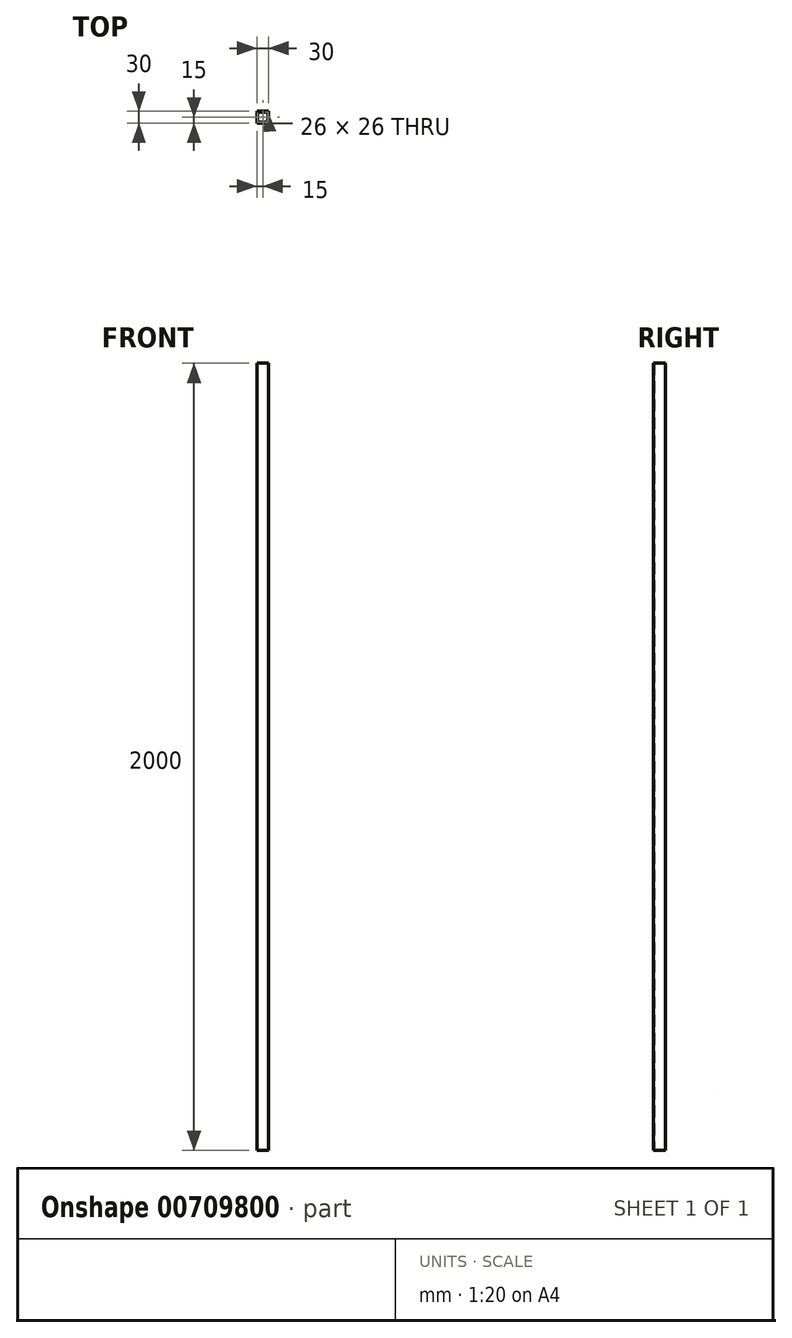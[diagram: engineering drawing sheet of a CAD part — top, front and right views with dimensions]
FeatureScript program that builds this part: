
annotation { "Feature Type Name" : "Feature", "Feature Type Description" : "" }
export const myFeature = defineFeature(function(context is Context, id is Id, definition is map)
    precondition{}
    {
        {
            var Q0;
            Q0=qCreatedBy(makeId("Top.planeOp"),FACE);
            var sketch = newSketch(context, id + "F0", { "sketchPlane" : qUnion([Q0])});
            skLineSegment(sketch, "E0.bottom", {"start": v(0, 0) * mm, "end": v(-30, 0) * mm});
            skLineSegment(sketch, "E0.top", {"start": v(0, 30) * mm, "end": v(-30, 30) * mm});
            skLineSegment(sketch, "E0.left", {"start": v(0, 0) * mm, "end": v(0, 30) * mm});
            skLineSegment(sketch, "E0.right", {"start": v(-30, 0) * mm, "end": v(-30, 30) * mm});
            skLineSegment(sketch, "E1.0", {"start": v(-28, 2) * mm, "end": v(-28, 28) * mm});
            skLineSegment(sketch, "E1.1", {"start": v(-2, 2) * mm, "end": v(-28, 2) * mm});
            skLineSegment(sketch, "E1.2", {"start": v(-2, 2) * mm, "end": v(-2, 28) * mm});
            skLineSegment(sketch, "E1.3", {"start": v(-2, 28) * mm, "end": v(-28, 28) * mm});
            skSolve(sketch);
        }
        {
            var Q0;
            Q0=makeQuery(id+"F0.imprint","IMPRINT",FACE,{"disambiguationData":[TD([[makeQuery(id+"F0.imprint","IMPRINT",EDGE,{"derivedFrom":sQuery(id+"F0.wireOp",EDGE,"E0.bottom")}),-1.0]])]});
            extrude(context, id + "F1", {"entities" : qUnion([Q0]), "depth" : 2000 * mm, "offsetDistance" : 25 * mm});
        }
    });
